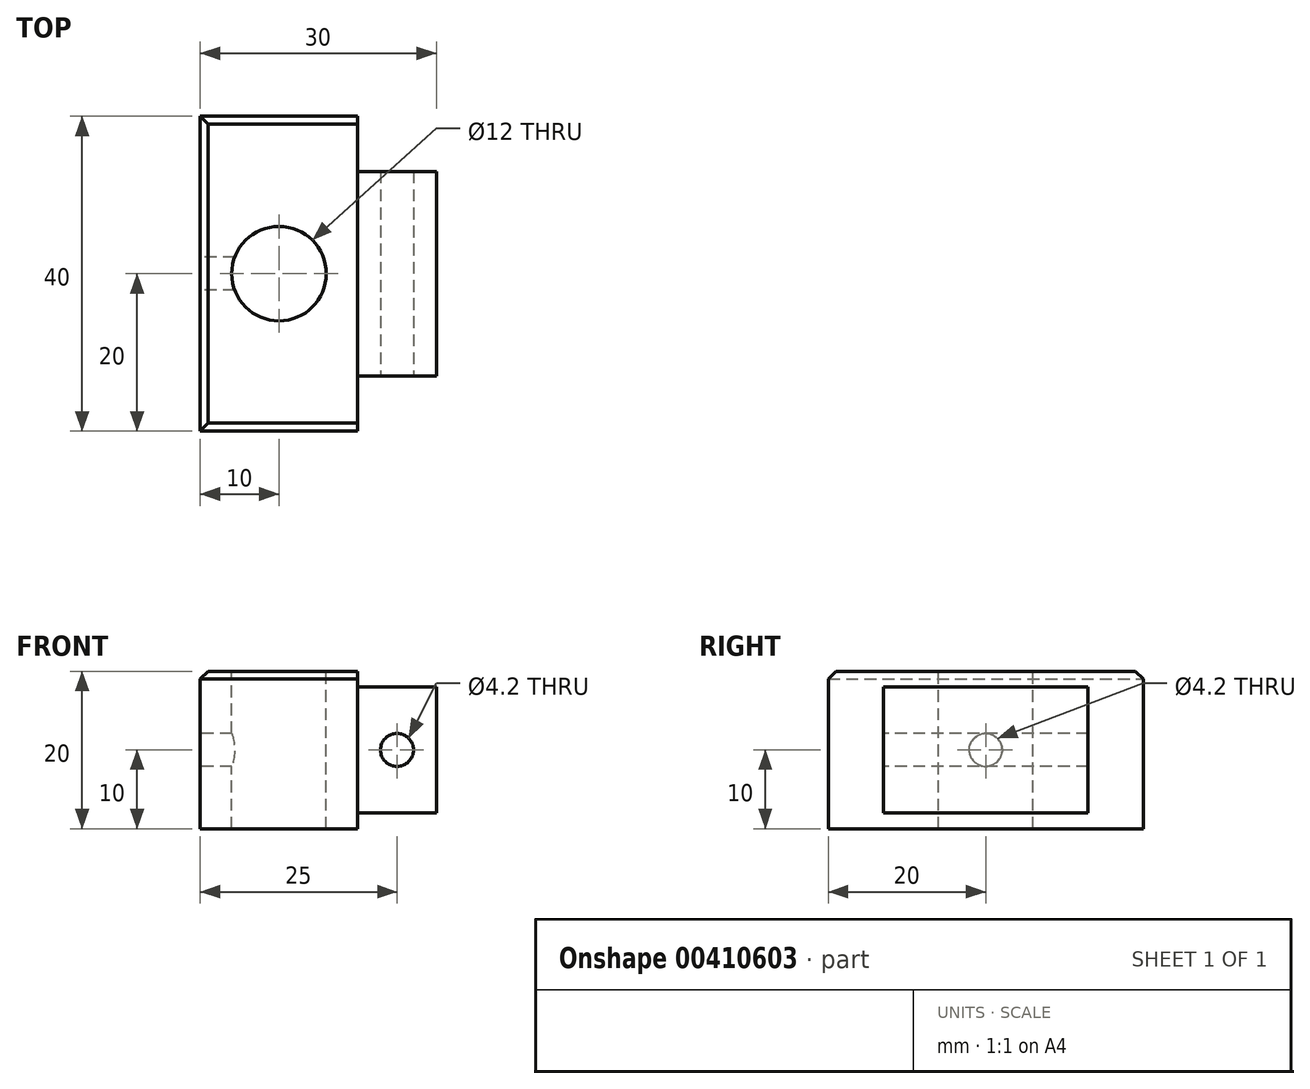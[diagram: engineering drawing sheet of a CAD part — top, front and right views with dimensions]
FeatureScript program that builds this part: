
annotation { "Feature Type Name" : "Feature", "Feature Type Description" : "" }
export const myFeature = defineFeature(function(context is Context, id is Id, definition is map)
    precondition{}
    {
        {
            var Q0;
            Q0=qCreatedBy(makeId("Top.planeOp"),FACE);
            var sketch = newSketch(context, id + "F0", { "sketchPlane" : qUnion([Q0])});
            skLineSegment(sketch, "E0.bottom", {"start": v(0, 0) * mm, "end": v(20, 0) * mm});
            skLineSegment(sketch, "E0.top", {"start": v(0, 40) * mm, "end": v(20, 40) * mm});
            skLineSegment(sketch, "E0.left", {"start": v(0, 0) * mm, "end": v(0, 40) * mm});
            skLineSegment(sketch, "E0.right", {"start": v(20, 0) * mm, "end": v(20, 40) * mm});
            skSolve(sketch);
        }
        {
            var Q0;
            Q0 = qSketchRegion(id + "F0", true);
            extrude(context, id + "F1", {"entities" : qUnion([Q0]), "depth" : 20 * mm});
        }
        {
            var Q0;
            Q0=makeQuery(id+"FvKnIAyj8Lz8nMk_1.boolean.opBoolean","MERGE",FACE,{"derivedFrom":[makeQuery(id+"F1.opExtrude","CAP_FACE",FACE,{"disambiguationData":[OSD([sQuery(id+"F0.wireOp",EDGE,"E0.bottom"),sQuery(id+"F0.wireOp",EDGE,"E0.top"),sQuery(id+"F0.wireOp",EDGE,"E0.left"),sQuery(id+"F0.wireOp",EDGE,"E0.right")])],"isStart":false}),makeQuery(id+"FvKnIAyj8Lz8nMk_1.opExtrude","SWEPT_FACE",FACE,{"disambiguationData":[OSD([sQuery(id+"FBW1Etj65JRndjI_1.wireOp",EDGE,"4T5Trhzw-LnXa-j9ia-rXul-RvbqkNwkaM5D.bottom")])]})]});
            var sketch = newSketch(context, id + "F2", { "sketchPlane" : qUnion([Q0])});
            skPoint(sketch, "E1", {"position": v(10, 20) * mm});
            skSolve(sketch);
        }
        {
            var Q0;
            Q0=sQuery(id+"F2.wireOp",VERTEX,"E1");
            var Q1;
            Q1=makeQuery(id+"F1.opExtrude","SWEPT_BODY",BODY,{"disambiguationData":[OSD([sQuery(id+"F0.wireOp",EDGE,"E0.bottom"),sQuery(id+"F0.wireOp",EDGE,"E0.top"),sQuery(id+"F0.wireOp",EDGE,"E0.left"),sQuery(id+"F0.wireOp",EDGE,"E0.right")])]});
            hole(context, id + "F3", {"style" : HoleStyle.SIMPLE, "endStyle" : HoleEndStyle.THROUGH, "standardTappedOrClearance" : lookupTablePath({ "standard" : "ISO", "size" : "12", "type" : "Drilled" }), "standardBlindInLast" : lookupTablePath({ "standard" : "ISO", "size" : "12", "type" : "Drilled" }), "holeDiameter" : 12 * mm, "isTappedThrough" : true, "tappedDepth" : 5.6 * mm, "tapClearance" : 3, "locations" : qUnion([Q0]), "scope" : qUnion([Q1])});
        }
        {
            var Q0;
            Q0=makeQuery(id+"F1.opExtrude","SWEPT_FACE",FACE,{"disambiguationData":[OSD([sQuery(id+"F0.wireOp",EDGE,"E0.left")])]});
            var sketch = newSketch(context, id + "F4", { "sketchPlane" : qUnion([Q0])});
            skPoint(sketch, "E2", {"position": v(-20, 10) * mm});
            skSolve(sketch);
        }
        {
            var Q0;
            Q0=sQuery(id+"F4.wireOp",VERTEX,"E2");
            var Q1;
            Q1=makeQuery(id+"F1.opExtrude","SWEPT_BODY",BODY,{"disambiguationData":[OSD([sQuery(id+"F0.wireOp",EDGE,"E0.bottom"),sQuery(id+"F0.wireOp",EDGE,"E0.top"),sQuery(id+"F0.wireOp",EDGE,"E0.left"),sQuery(id+"F0.wireOp",EDGE,"E0.right")])]});
            hole(context, id + "F5", {"style" : HoleStyle.SIMPLE, "endStyle" : HoleEndStyle.BLIND, "standardTappedOrClearance" : lookupTablePath({ "standard" : "ISO", "engagement" : "75%", "pitch" : "0.8 mm", "size" : "M5", "type" : "Tapped" }), "standardBlindInLast" : lookupTablePath({ "standard" : "ISO", "engagement" : "75%", "pitch" : "0.8 mm", "size" : "M5", "type" : "Tapped" }), "holeDiameter" : 4.2 * mm, "showTappedDepth" : true, "holeDepth" : 5 * mm, "isTappedThrough" : true, "tappedDepth" : 2.6 * mm, "tapClearance" : 3, "locations" : qUnion([Q0]), "scope" : qUnion([Q1]), "majorDiameter" : 5 * mm});
        }
        {
            var Q0;
            Q0=makeQuery(id+"F1.opExtrude","SWEPT_FACE",FACE,{"disambiguationData":[OSD([sQuery(id+"F0.wireOp",EDGE,"E0.bottom")])]});
            var sketch = newSketch(context, id + "F6", { "sketchPlane" : qUnion([Q0])});
            skPoint(sketch, "E3", {"position": v(25, 10) * mm});
            skSolve(sketch);
        }
        {
            var Q0;
            Q0=sQuery(id+"F6.wireOp",VERTEX,"E3");
            var Q1;
            Q1=makeQuery(id+"F1.opExtrude","SWEPT_BODY",BODY,{"disambiguationData":[OSD([sQuery(id+"F0.wireOp",EDGE,"E0.bottom"),sQuery(id+"F0.wireOp",EDGE,"E0.top"),sQuery(id+"F0.wireOp",EDGE,"E0.left"),sQuery(id+"F0.wireOp",EDGE,"E0.right")])]});
            hole(context, id + "F7", {"style" : HoleStyle.SIMPLE, "endStyle" : HoleEndStyle.THROUGH, "standardTappedOrClearance" : lookupTablePath({ "standard" : "ISO", "engagement" : "75%", "pitch" : "0.8 mm", "size" : "M5", "type" : "Tapped" }), "standardBlindInLast" : lookupTablePath({ "standard" : "ISO", "engagement" : "75%", "pitch" : "0.8 mm", "size" : "M5", "type" : "Tapped" }), "holeDiameter" : 4.2 * mm, "showTappedDepth" : true, "isTappedThrough" : true, "tappedDepth" : 2.6 * mm, "tapClearance" : 3, "locations" : qUnion([Q0]), "scope" : qUnion([Q1]), "majorDiameter" : 5 * mm});
        }
        {
            var Q0;
            Q0=makeQuery(id+"F1.opExtrude","CAP_EDGE",EDGE,{"disambiguationData":[OSD([sQuery(id+"F0.wireOp",EDGE,"E0.bottom")])],"isStart":false});
            var Q1;
            Q1=makeQuery(id+"F1.opExtrude","CAP_EDGE",EDGE,{"disambiguationData":[OSD([sQuery(id+"F0.wireOp",EDGE,"E0.left")])],"isStart":false});
            var Q2;
            Q2=makeQuery(id+"F1.opExtrude","CAP_EDGE",EDGE,{"disambiguationData":[OSD([sQuery(id+"F0.wireOp",EDGE,"E0.top")])],"isStart":false});
            chamfer(context, id + "F8", {"entities" : qUnion([Q0, Q1, Q2]), "width" : 1 * mm, "tangentPropagation" : true});
        }
        {
            var Q0;
            Q0=makeQuery(id+"F1.opExtrude","SWEPT_FACE",FACE,{"disambiguationData":[OSD([sQuery(id+"F0.wireOp",EDGE,"E0.right")])]});
            var sketch = newSketch(context, id + "F9", { "sketchPlane" : qUnion([Q0])});
            skLineSegment(sketch, "E4.bottom", {"start": v(7, 18) * mm, "end": v(33, 18) * mm});
            skLineSegment(sketch, "E4.top", {"start": v(7, 2) * mm, "end": v(33, 2) * mm});
            skLineSegment(sketch, "E4.left", {"start": v(7, 18) * mm, "end": v(7, 2) * mm});
            skLineSegment(sketch, "E4.right", {"start": v(33, 18) * mm, "end": v(33, 2) * mm});
            skSolve(sketch);
        }
        {
            var Q0;
            Q0=makeQuery(id+"F9.imprint","IMPRINT",FACE,{"disambiguationData":[TD([[makeQuery(id+"F9.imprint","IMPRINT",EDGE,{"derivedFrom":sQuery(id+"F9.wireOp",EDGE,"E4.bottom")}),-1.0]])]});
            extrude(context, id + "F10", {"entities" : qUnion([Q0]), "operationType" : NewBodyOperationType.ADD, "depth" : 10 * mm});
        }
        {
            var Q0;
            Q0=makeQuery(id+"F10.opExtrude","SWEPT_FACE",FACE,{"disambiguationData":[OSD([sQuery(id+"F9.wireOp",EDGE,"E4.left")])]});
            var sketch = newSketch(context, id + "F11", { "sketchPlane" : qUnion([Q0])});
            skPoint(sketch, "E5", {"position": v(25, 10) * mm});
            skSolve(sketch);
        }
        {
            var Q0;
            Q0=sQuery(id+"F11.wireOp",VERTEX,"E5");
            var Q1;
            Q1=makeQuery(id+"F1.opExtrude","SWEPT_BODY",BODY,{"disambiguationData":[OSD([sQuery(id+"F0.wireOp",EDGE,"E0.bottom"),sQuery(id+"F0.wireOp",EDGE,"E0.top"),sQuery(id+"F0.wireOp",EDGE,"E0.left"),sQuery(id+"F0.wireOp",EDGE,"E0.right")])]});
            hole(context, id + "F12", {"style" : HoleStyle.SIMPLE, "endStyle" : HoleEndStyle.THROUGH, "standardTappedOrClearance" : lookupTablePath({ "standard" : "ISO", "engagement" : "75%", "pitch" : "0.8 mm", "size" : "M5", "type" : "Tapped" }), "standardBlindInLast" : lookupTablePath({ "standard" : "ISO", "engagement" : "75%", "pitch" : "0.8 mm", "size" : "M5", "type" : "Tapped" }), "holeDiameter" : 4.2 * mm, "showTappedDepth" : true, "isTappedThrough" : true, "tappedDepth" : 5 * mm, "tapClearance" : 3, "locations" : qUnion([Q0]), "scope" : qUnion([Q1]), "majorDiameter" : 5 * mm});
        }
    });
